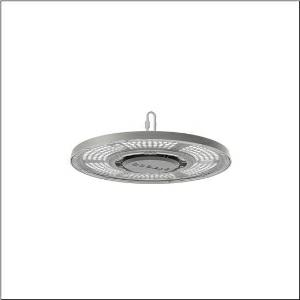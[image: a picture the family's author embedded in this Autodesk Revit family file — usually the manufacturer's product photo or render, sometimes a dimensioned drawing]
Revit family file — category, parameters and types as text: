
# Revit family: highbay_31-s_51hc417a4jmb
name_source: partatom
category: Lighting Fixtures
units: mm (PartAtom-declared; Revit-internal decimal feet)

## family parameters
Cut with Voids When Loaded = No
Host = Face
Light Source = No
Part Type = Normal
Room Calculation Point = No
Round Connector Dimension = Use Diameter
Shared = No

## types (1)
- Highbay 31-S (1 x LED, 20000 lm, 134 W, 4000K)
    Apparent Load = 134 VA
    CIE Flux Codes = 95 98 100 100 100
    Color Rendering = 80
    Color Temperature = 4000K
    Default Elevation = 1800 mm
    Description = Highbay 31-S, LED high bay luminaire, primary light control with lens, of PC, primary optical cover: cover panel, of PC, transparent, light emission: direct distribution, primary light characteristic: rotationally symmetric, installation type: suspended mounting, surface-mounted, LED, rated luminous flux: 20.000lm, luminous efficacy: 150lm/W, light colour: 840, colour temperature: 4000K, control gear: ECG, with cable, 3x 1.0mm², free wire ends, mains connection: 220..240V, AC/DC, 0/50..60Hz, cable length: 1,5m, rated input power: 134W, housing, rotationally symmetric, of diecast aluminium, grey aluminium (RAL 9007), diameter: 339mm, protection rating (complete): IP65, insulation class (complete): insulation class I (protective earthing), certification: CE, ENEC, UKCA, protection symbol: D, impact resistance: IK08, permissible operating ambient temperature: -30..+45°C, standard: EN 60598-2-22, EN 60598, corresponds to IFS (International Featured Standards) requirements for safety and quality in the food industry, packaging unit: 1 piece
    Height = 141 mm
    Lamp = 1 x LED
    Lamp Light Flux = 20000 lm
    Lamp Power = 134 W
    Lamp count = 1
    Length = 339 mm
    Luminous efficacy = 149 lm/W
    Manufacturer = Siteco
    ModVariant = No
    Model = 51HC417A4JMB
    Mounting Place = Ceiling
    Mounting Type = Pendant
    Number of Poles = 1
    OnlyDefault = Yes
    Power Factor = 1
    Product Name = Highbay 31-S
    Product group = LED high bay luminaire
    ProductGroupID = 903
    Protection Class = Protection class I
    Protection Degree = IP 65
    RLX_Detail_Level = 1
    RlxData = <blob elided: 107169 chars, md5=5f07a238>
    Socket = socket
    Standby Power = 0 W
    System Light Flux = 20000 lm
    System Power = 134 W
    Type Comments = Product without accessories
    Type Image = l_1007237.jpg
    URL = http://relux.com
    VarID = ---
    Voltage = 0 V
    Weight = 0.00 kg
    Width = 0 mm  [stored 0 ft]

note: [stored X ft] marks values corroborated as IEEE doubles in the binary element streams (Revit-internal decimal feet)

## geometry (parser evidence)
native form markers: Blend x4, Sweep x10
no freeform markers — native parametric forms only
